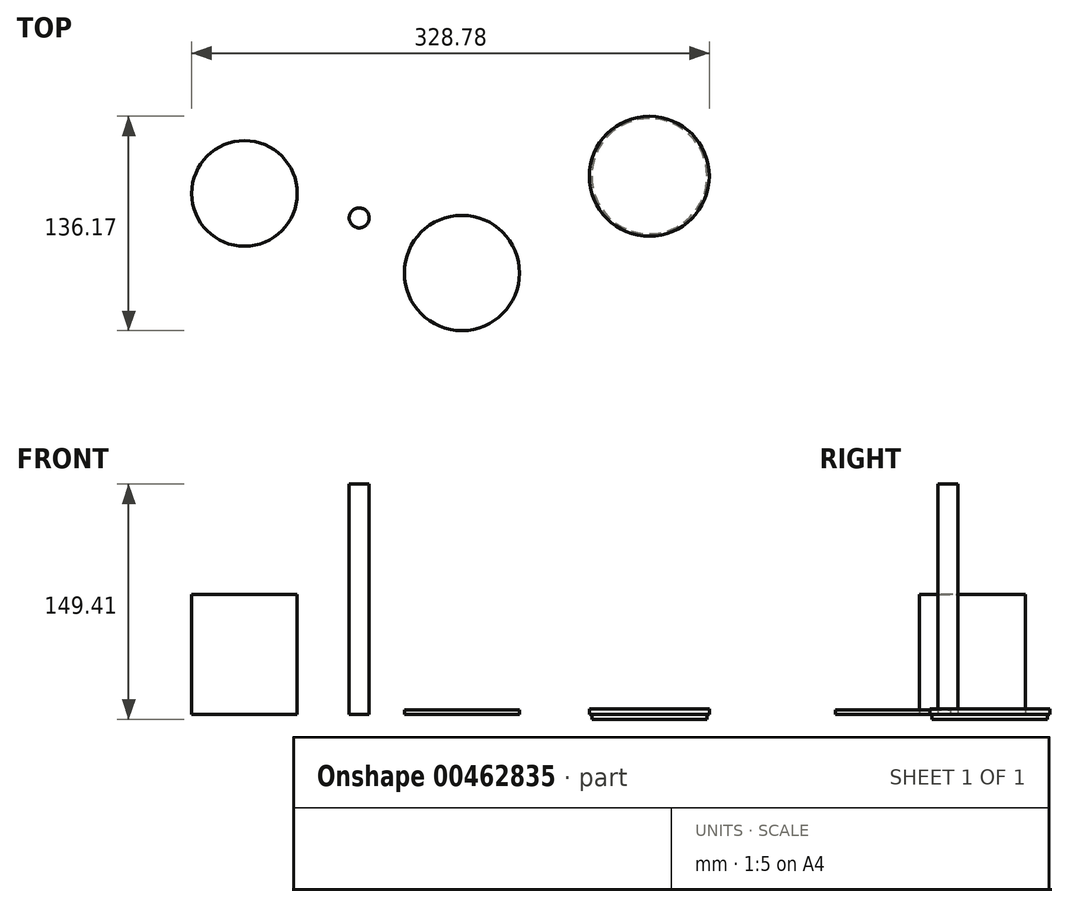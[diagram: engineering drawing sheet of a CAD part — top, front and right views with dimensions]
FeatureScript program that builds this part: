
annotation { "Feature Type Name" : "Feature", "Feature Type Description" : "" }
export const myFeature = defineFeature(function(context is Context, id is Id, definition is map)
    precondition{}
    {
        {
            var Q0;
            Q0=qCreatedBy(makeId("Top.planeOp"),FACE);
            var sketch = newSketch(context, id + "F0", { "sketchPlane" : qUnion([Q0])});
            skCircle(sketch, "E0", {"center": v(0, 0) * mm, "radius": 36.6 * mm});
            skSolve(sketch);
        }
        {
            var Q0;
            Q0=makeQuery(id+"F0.imprint","IMPRINT",FACE,{"disambiguationData":[TD([[makeQuery(id+"F0.imprint","IMPRINT",EDGE,{"derivedFrom":sQuery(id+"F0.wireOp",EDGE,"E0")}),1.0]])]});
            extrude(context, id + "F1", {"entities" : qUnion([Q0]), "depth" : 3 * mm});
        }
        {
            var Q0;
            Q0=qCreatedBy(makeId("Top.planeOp"),FACE);
            var sketch = newSketch(context, id + "F2", { "sketchPlane" : qUnion([Q0])});
            skCircle(sketch, "E1", {"center": v(-65.22, 34.98) * mm, "radius": 6.35 * mm});
            skSolve(sketch);
        }
        {
            var Q0;
            Q0=makeQuery(id+"F2.imprint","IMPRINT",FACE,{"disambiguationData":[TD([[makeQuery(id+"F2.imprint","IMPRINT",EDGE,{"derivedFrom":sQuery(id+"F2.wireOp",EDGE,"E1")}),1.0]])]});
            extrude(context, id + "F3", {"entities" : qUnion([Q0]), "depth" : 146.4 * mm});
        }
        {
            var Q0;
            Q0=qCreatedBy(makeId("Top.planeOp"),FACE);
            var sketch = newSketch(context, id + "F4", { "sketchPlane" : qUnion([Q0])});
            skCircle(sketch, "E2", {"center": v(119.06, 61.47) * mm, "radius": 38.1 * mm});
            skCircle(sketch, "E3", {"center": v(119.06, 61.47) * mm, "radius": 36.6 * mm});
            skSolve(sketch);
        }
        {
            var Q0;
            Q0=makeQuery(id+"F4.imprint","IMPRINT",FACE,{"disambiguationData":[TD([[makeQuery(id+"F4.imprint","IMPRINT",EDGE,{"derivedFrom":sQuery(id+"F4.wireOp",EDGE,"E3")}),1.0]])]});
            extrude(context, id + "F5", {"entities" : qUnion([Q0]), "oppositeDirection" : true, "depth" : 3 * mm});
        }
        {
            var Q0;
            Q0 = qSketchRegion(id + "F4", true);
            var Q1;
            Q1=makeQuery(id+"F5.opExtrude","CAP_FACE",FACE,{"disambiguationData":[OSD([sQuery(id+"F4.wireOp",EDGE,"E3")])],"isStart":true});
            extrude(context, id + "F6", {"entities" : qUnion([Q0, Q1]), "operationType" : NewBodyOperationType.ADD, "depth" : 3.45 * mm});
        }
        {
            var Q0;
            Q0=qCreatedBy(makeId("Top.planeOp"),FACE);
            var sketch = newSketch(context, id + "F7", { "sketchPlane" : qUnion([Q0])});
            skCircle(sketch, "E4", {"center": v(-138.1, 50.5) * mm, "radius": 33.53 * mm});
            skSolve(sketch);
        }
        {
            var Q0;
            Q0=makeQuery(id+"F7.imprint","IMPRINT",FACE,{"disambiguationData":[TD([[makeQuery(id+"F7.imprint","IMPRINT",EDGE,{"derivedFrom":sQuery(id+"F7.wireOp",EDGE,"E4")}),1.0]])]});
            extrude(context, id + "F8", {"entities" : qUnion([Q0]), "depth" : 76.2 * mm});
        }
    });
